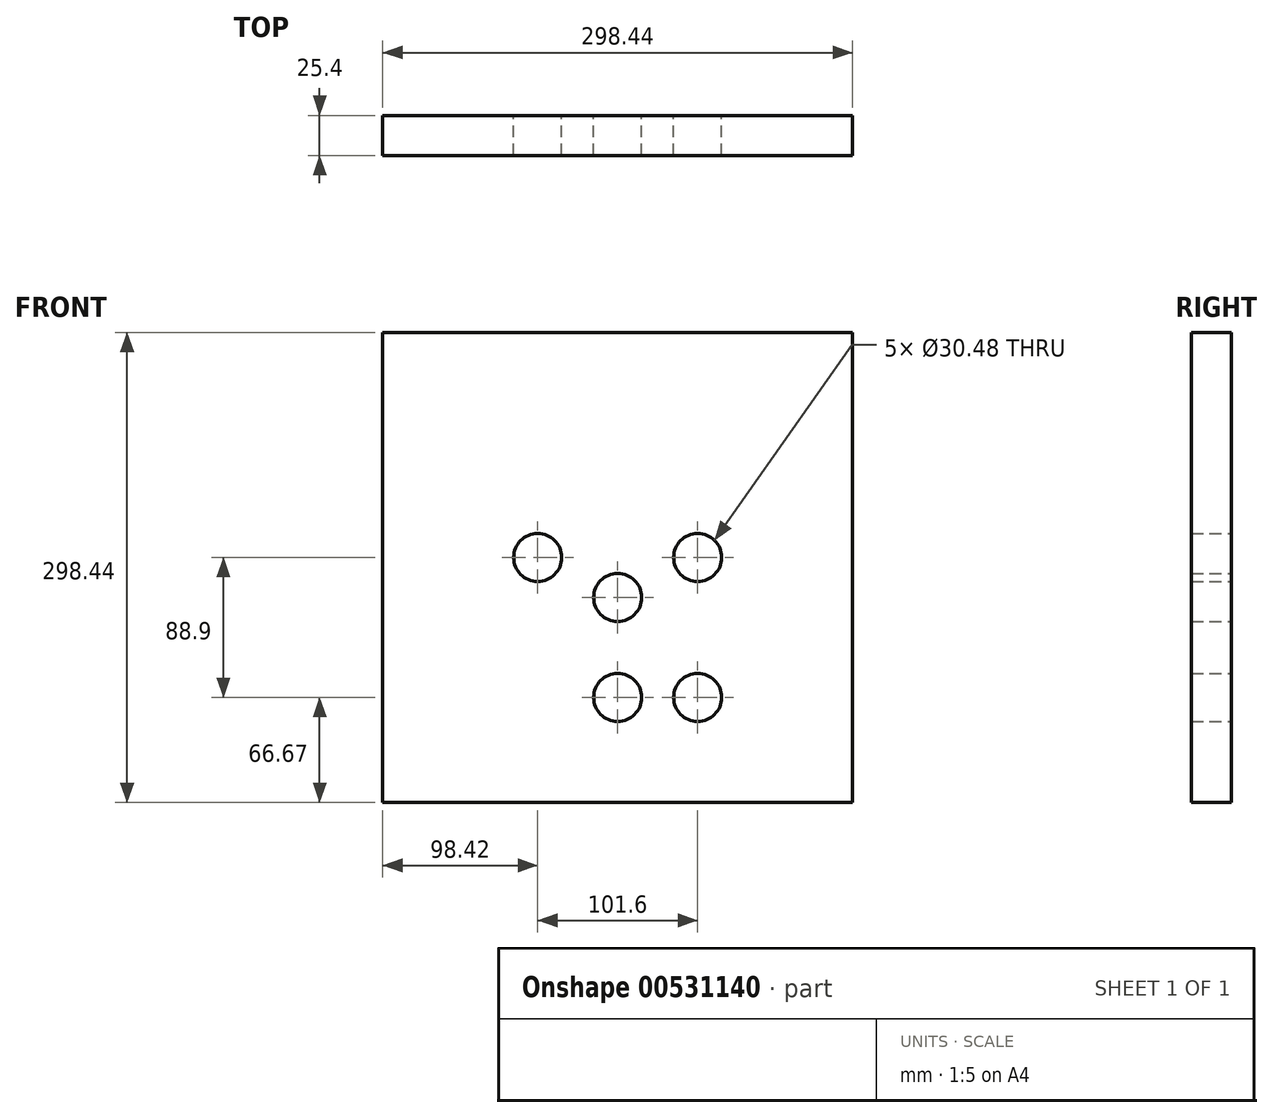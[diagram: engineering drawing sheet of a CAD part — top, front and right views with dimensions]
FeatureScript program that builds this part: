
annotation { "Feature Type Name" : "Feature", "Feature Type Description" : "" }
export const myFeature = defineFeature(function(context is Context, id is Id, definition is map)
    precondition{}
    {
        {
            var Q0;
            Q0=qCreatedBy(makeId("Front.planeOp"),FACE);
            var sketch = newSketch(context, id + "F0", { "sketchPlane" : qUnion([Q0])});
            skLineSegment(sketch, "E0.bottom", {"start": v(149.22, 149.23) * mm, "end": v(-149.22, 149.23) * mm});
            skLineSegment(sketch, "E0.top", {"start": v(149.22, -149.23) * mm, "end": v(-149.23, -149.23) * mm});
            skLineSegment(sketch, "E0.left", {"start": v(149.23, 149.23) * mm, "end": v(149.22, -149.23) * mm});
            skLineSegment(sketch, "E0.right", {"start": v(-149.22, 149.23) * mm, "end": v(-149.23, -149.23) * mm});
            skCircle(sketch, "E1", {"center": v(-50.8, 6.35) * mm, "radius": 15.24 * mm});
            skCircle(sketch, "E2", {"center": v(0, -19.05) * mm, "radius": 15.24 * mm});
            skCircle(sketch, "E3", {"center": v(0, -82.55) * mm, "radius": 15.24 * mm});
            skCircle(sketch, "E4", {"center": v(50.8, -82.55) * mm, "radius": 15.24 * mm});
            skCircle(sketch, "E5", {"center": v(50.8, 6.35) * mm, "radius": 15.24 * mm});
            skPoint(sketch, "E6", {"position": v(-149.22, 0) * mm});
            skPoint(sketch, "E7", {"position": v(0, -149.23) * mm});
            skLineSegment(sketch, "E8", {"start": v(-149.22, 0) * mm, "end": v(149.22, 0) * mm, "construction": true});
            skLineSegment(sketch, "E9", {"start": v(0, -149.23) * mm, "end": v(0, 149.23) * mm, "construction": true});
            skPoint(sketch, "E10", {"position": v(0, 0) * mm});
            skLineSegment(sketch, "E11.bottom", {"start": v(-28.13, 29.02) * mm, "end": v(-73.47, 29.02) * mm, "construction": true});
            skLineSegment(sketch, "E11.top", {"start": v(-28.13, -16.32) * mm, "end": v(-73.47, -16.32) * mm, "construction": true});
            skLineSegment(sketch, "E11.left", {"start": v(-28.13, 29.02) * mm, "end": v(-28.13, -16.32) * mm, "construction": true});
            skLineSegment(sketch, "E11.right", {"start": v(-73.47, 29.02) * mm, "end": v(-73.47, -16.32) * mm, "construction": true});
            skLineSegment(sketch, "E12.bottom", {"start": v(22.67, 3.62) * mm, "end": v(-22.67, 3.62) * mm, "construction": true});
            skLineSegment(sketch, "E12.top", {"start": v(22.67, -41.72) * mm, "end": v(-22.67, -41.72) * mm, "construction": true});
            skLineSegment(sketch, "E12.left", {"start": v(22.67, 3.62) * mm, "end": v(22.67, -41.72) * mm, "construction": true});
            skLineSegment(sketch, "E12.right", {"start": v(-22.67, 3.62) * mm, "end": v(-22.67, -41.72) * mm, "construction": true});
            skLineSegment(sketch, "E13.bottom", {"start": v(73.47, 29.02) * mm, "end": v(28.13, 29.02) * mm, "construction": true});
            skLineSegment(sketch, "E13.top", {"start": v(73.47, -16.32) * mm, "end": v(28.13, -16.32) * mm, "construction": true});
            skLineSegment(sketch, "E13.left", {"start": v(73.47, 29.02) * mm, "end": v(73.47, -16.32) * mm, "construction": true});
            skLineSegment(sketch, "E13.right", {"start": v(28.13, 29.02) * mm, "end": v(28.13, -16.32) * mm, "construction": true});
            skSolve(sketch);
        }
        {
            var Q0;
            Q0=qSketchRegion(id+"F0",true);
            extrude(context, id + "F1", {"entities" : qUnion([Q0]), "depth" : 25.4 * mm, "offsetDistance" : 25.4 * mm});
        }
    });
